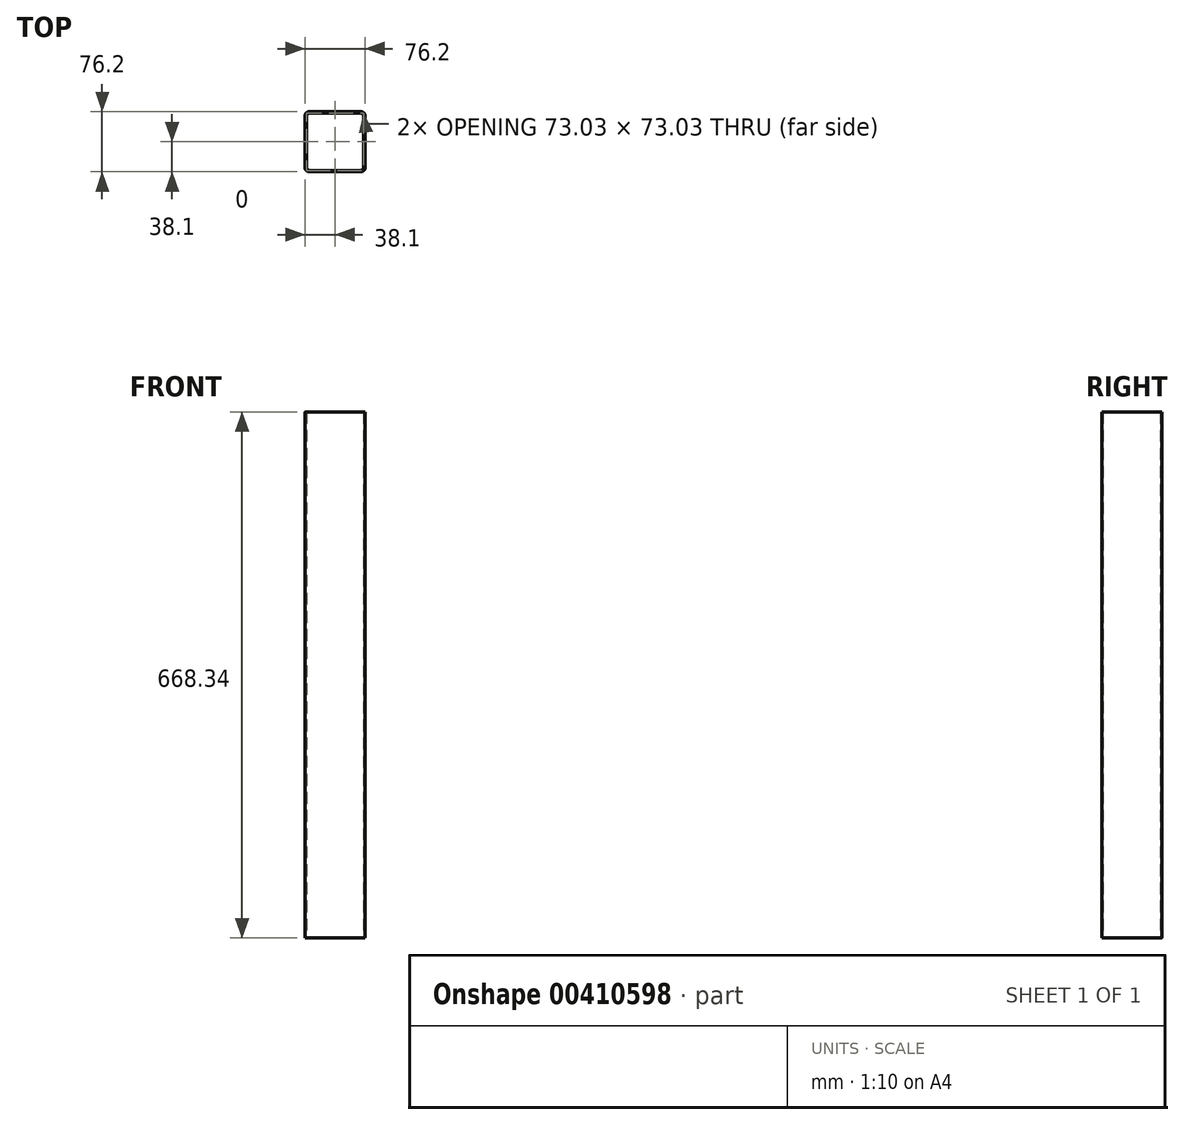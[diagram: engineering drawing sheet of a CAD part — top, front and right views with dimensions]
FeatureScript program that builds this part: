
annotation { "Feature Type Name" : "Feature", "Feature Type Description" : "" }
export const myFeature = defineFeature(function(context is Context, id is Id, definition is map)
    precondition{}
    {
        {
            var Q0;
            Q0=qCreatedBy(makeId("Top.planeOp"),FACE);
            var sketch = newSketch(context, id + "F0", { "sketchPlane" : qUnion([Q0])});
            skLineSegment(sketch, "E0.bottom", {"start": v(38.1, 38.1) * mm, "end": v(-38.1, 38.1) * mm});
            skLineSegment(sketch, "E0.top", {"start": v(38.1, -38.1) * mm, "end": v(-38.1, -38.1) * mm});
            skLineSegment(sketch, "E0.left", {"start": v(38.1, 38.1) * mm, "end": v(38.1, -38.1) * mm});
            skLineSegment(sketch, "E0.right", {"start": v(-38.1, 38.1) * mm, "end": v(-38.1, -38.1) * mm});
            skPoint(sketch, "E0.middle", {"position": v(0, 0) * mm});
            skLineSegment(sketch, "E1.bottom", {"start": v(36.51, 36.51) * mm, "end": v(-36.51, 36.51) * mm});
            skLineSegment(sketch, "E1.top", {"start": v(36.51, -36.51) * mm, "end": v(-36.51, -36.51) * mm});
            skLineSegment(sketch, "E1.left", {"start": v(36.51, 36.51) * mm, "end": v(36.51, -36.51) * mm});
            skLineSegment(sketch, "E1.right", {"start": v(-36.51, 36.51) * mm, "end": v(-36.51, -36.51) * mm});
            skSolve(sketch);
        }
        {
            var Q0;
            Q0=makeQuery(id+"F0.imprint","IMPRINT",FACE,{"disambiguationData":[TD([[makeQuery(id+"F0.imprint","IMPRINT",EDGE,{"derivedFrom":sQuery(id+"F0.wireOp",EDGE,"E0.bottom")}),1.0]])]});
            extrude(context, id + "F1", {"entities" : qUnion([Q0]), "depth" : 668.34 * mm});
        }
        {
            var Q0;
            Q0=makeQuery(id+"F1.opExtrude","SWEPT_EDGE",EDGE,{"disambiguationData":[OSD([sQuery(id+"F0.wireOp",EDGE,"E0.top"),sQuery(id+"F0.wireOp",EDGE,"E0.right")])]});
            fillet(context, id + "F2", {"entities" : qUnion([Q0]), "radius" : 5.08 * mm, "tangentPropagation" : true, "allowEdgeOverflow" : false});
        }
        {
            var Q0;
            Q0=makeQuery(id+"F1.opExtrude","SWEPT_EDGE",EDGE,{"disambiguationData":[OSD([sQuery(id+"F0.wireOp",EDGE,"E0.top"),sQuery(id+"F0.wireOp",EDGE,"E0.left")])]});
            var Q1;
            Q1=makeQuery(id+"F1.opExtrude","SWEPT_EDGE",EDGE,{"disambiguationData":[OSD([sQuery(id+"F0.wireOp",EDGE,"E0.bottom"),sQuery(id+"F0.wireOp",EDGE,"E0.left")])]});
            fillet(context, id + "F3", {"entities" : qUnion([Q0, Q1]), "radius" : 5.08 * mm, "tangentPropagation" : true, "allowEdgeOverflow" : false});
        }
        {
            var Q0;
            Q0=makeQuery(id+"F1.opExtrude","SWEPT_EDGE",EDGE,{"disambiguationData":[OSD([sQuery(id+"F0.wireOp",EDGE,"E1.bottom"),sQuery(id+"F0.wireOp",EDGE,"E1.right")])]});
            fillet(context, id + "F4", {"entities" : qUnion([Q0]), "radius" : 5.08 * mm, "tangentPropagation" : true, "allowEdgeOverflow" : false});
        }
        {
            var Q0;
            Q0=makeQuery(id+"F1.opExtrude","SWEPT_EDGE",EDGE,{"disambiguationData":[OSD([sQuery(id+"F0.wireOp",EDGE,"E0.bottom"),sQuery(id+"F0.wireOp",EDGE,"E0.right")])]});
            var Q1;
            Q1=makeQuery(id+"F1.opExtrude","SWEPT_EDGE",EDGE,{"disambiguationData":[OSD([sQuery(id+"F0.wireOp",EDGE,"E1.top"),sQuery(id+"F0.wireOp",EDGE,"E1.left")])]});
            fillet(context, id + "F5", {"entities" : qUnion([Q0, Q1]), "radius" : 5.08 * mm, "tangentPropagation" : true, "allowEdgeOverflow" : false});
        }
        {
            var Q0;
            Q0=makeQuery(id+"F1.opExtrude","SWEPT_EDGE",EDGE,{"disambiguationData":[OSD([sQuery(id+"F0.wireOp",EDGE,"E1.top"),sQuery(id+"F0.wireOp",EDGE,"E1.right")])]});
            fillet(context, id + "F6", {"entities" : qUnion([Q0]), "radius" : 5.08 * mm, "tangentPropagation" : true, "allowEdgeOverflow" : false});
        }
        {
            var Q0;
            Q0=makeQuery(id+"F1.opExtrude","SWEPT_EDGE",EDGE,{"disambiguationData":[OSD([sQuery(id+"F0.wireOp",EDGE,"E1.bottom"),sQuery(id+"F0.wireOp",EDGE,"E1.left")])]});
            fillet(context, id + "F7", {"entities" : qUnion([Q0]), "radius" : 5.08 * mm, "tangentPropagation" : true, "allowEdgeOverflow" : false});
        }
    });
